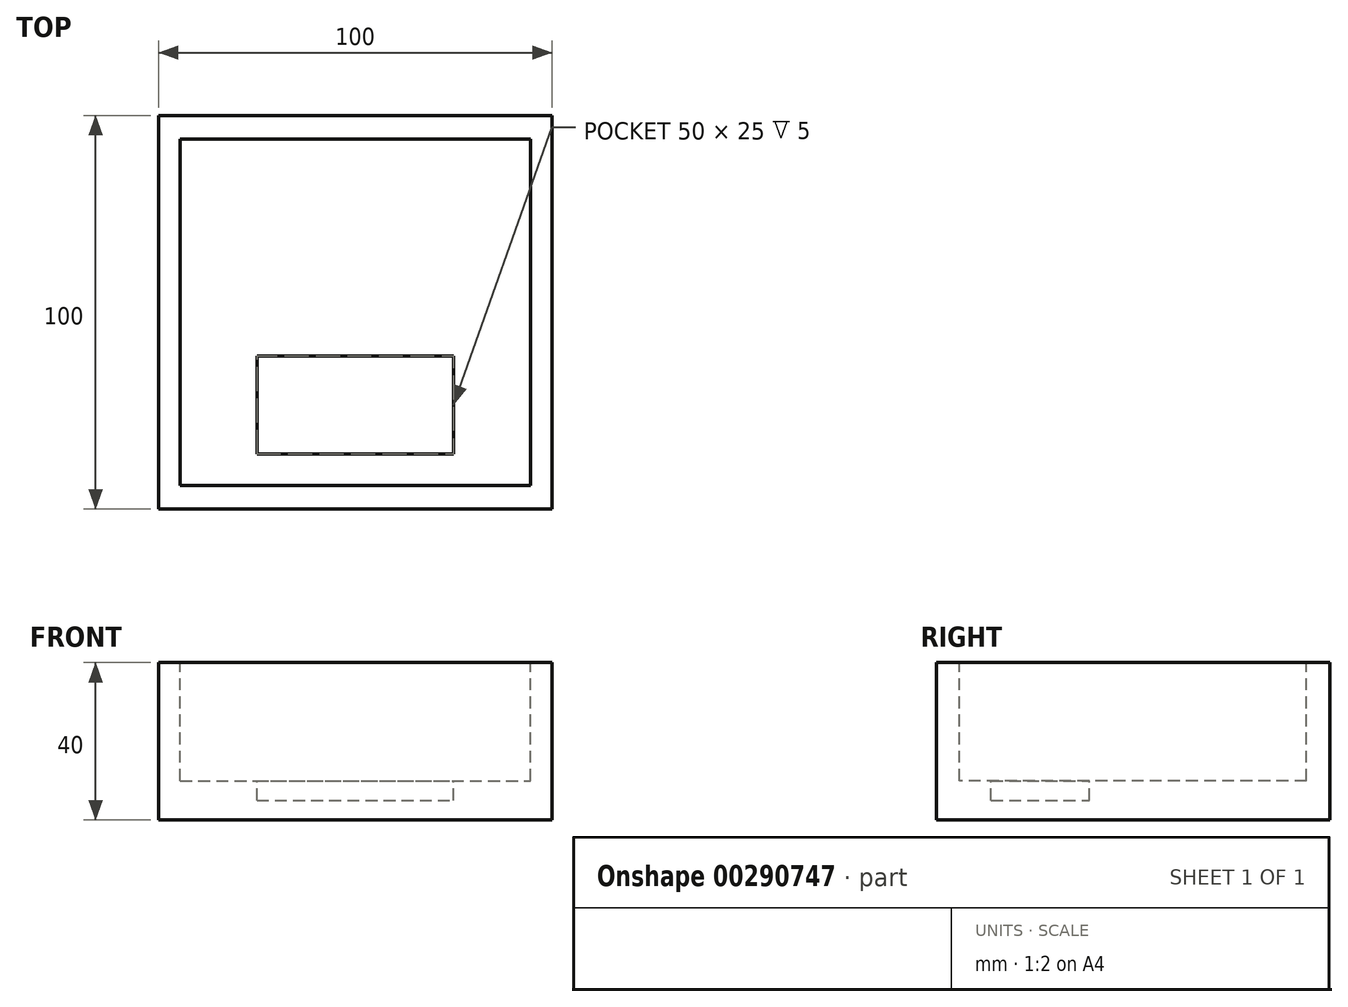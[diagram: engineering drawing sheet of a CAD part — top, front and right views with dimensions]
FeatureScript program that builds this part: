
annotation { "Feature Type Name" : "Feature", "Feature Type Description" : "" }
export const myFeature = defineFeature(function(context is Context, id is Id, definition is map)
    precondition{}
    {
        {
            var Q0;
            Q0=qCreatedBy(makeId("Top.planeOp"),FACE);
            var sketch = newSketch(context, id + "F0", { "sketchPlane" : qUnion([Q0])});
            skLineSegment(sketch, "E0.bottom", {"start": v(-50, 50) * mm, "end": v(50, 50) * mm});
            skLineSegment(sketch, "E0.top", {"start": v(-50, -50) * mm, "end": v(50, -50) * mm});
            skLineSegment(sketch, "E0.left", {"start": v(-50, 50) * mm, "end": v(-50, -50) * mm});
            skLineSegment(sketch, "E0.right", {"start": v(50, 50) * mm, "end": v(50, -50) * mm});
            skPoint(sketch, "E0.middle", {"position": v(0, 0) * mm});
            skSolve(sketch);
        }
        {
            var Q0;
            Q0=makeQuery(id+"F0.imprint","IMPRINT",FACE,{"disambiguationData":[TD([[makeQuery(id+"F0.imprint","IMPRINT",EDGE,{"derivedFrom":sQuery(id+"F0.wireOp",EDGE,"E0.bottom")}),-1.0]])]});
            extrude(context, id + "F1", {"entities" : qUnion([Q0]), "oppositeDirection" : true, "depth" : 40 * mm});
        }
        {
            var Q0;
            Q0=makeQuery(id+"F0.imprint","IMPRINT",FACE,{"disambiguationData":[TD([[makeQuery(id+"F0.imprint","IMPRINT",EDGE,{"derivedFrom":sQuery(id+"F0.wireOp",EDGE,"E0.bottom")}),-1.0]])]});
            var sketch = newSketch(context, id + "F2", { "sketchPlane" : qUnion([Q0])});
            skLineSegment(sketch, "E1.bottom", {"start": v(-44.48, 44.06) * mm, "end": v(44.48, 44.06) * mm});
            skLineSegment(sketch, "E1.top", {"start": v(-44.48, -44.06) * mm, "end": v(44.48, -44.06) * mm});
            skLineSegment(sketch, "E1.left", {"start": v(-44.48, 44.06) * mm, "end": v(-44.48, -44.06) * mm});
            skLineSegment(sketch, "E1.right", {"start": v(44.48, 44.06) * mm, "end": v(44.48, -44.06) * mm});
            skPoint(sketch, "E1.middle", {"position": v(0, 0) * mm});
            skSolve(sketch);
        }
        {
            var Q0;
            Q0 = qSketchRegion(id + "F2", true);
            extrude(context, id + "F3", {"entities" : qUnion([Q0]), "operationType" : NewBodyOperationType.REMOVE, "oppositeDirection" : true, "depth" : 30 * mm});
        }
        {
            var Q0;
            Q0=qCreatedBy(makeId("Top.planeOp"),FACE);
            var sketch = newSketch(context, id + "F4", { "sketchPlane" : qUnion([Q0])});
            skLineSegment(sketch, "E2.bottom", {"start": v(-25, -36.06) * mm, "end": v(25, -36.06) * mm});
            skLineSegment(sketch, "E2.top", {"start": v(-25, -11.06) * mm, "end": v(25, -11.06) * mm});
            skLineSegment(sketch, "E2.left", {"start": v(-25, -36.06) * mm, "end": v(-25, -11.06) * mm});
            skLineSegment(sketch, "E2.right", {"start": v(25, -36.06) * mm, "end": v(25, -11.06) * mm});
            skPoint(sketch, "E3", {"position": v(0, -36.06) * mm});
            skSolve(sketch);
        }
        {
            var Q0;
            Q0=makeQuery(id+"F4.imprint","IMPRINT",FACE,{"disambiguationData":[TD([[makeQuery(id+"F4.imprint","IMPRINT",EDGE,{"derivedFrom":sQuery(id+"F4.wireOp",EDGE,"E2.bottom")}),1.0]])]});
            extrude(context, id + "F5", {"entities" : qUnion([Q0]), "operationType" : NewBodyOperationType.REMOVE, "oppositeDirection" : true, "depth" : 35 * mm});
        }
    });
